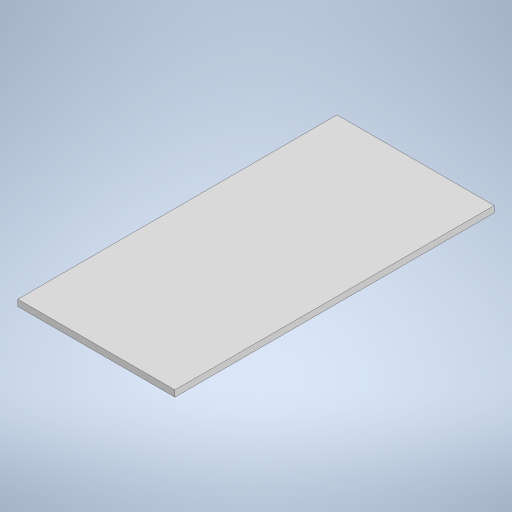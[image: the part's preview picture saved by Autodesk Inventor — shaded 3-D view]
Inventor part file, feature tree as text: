
AUTODESK INVENTOR PART (.ipt)
format: ipt  version: 2024 (Build 280153000, 153)  size: 204,800 bytes
history: native  units: mm
features: extrude x1, sketch x1
ambient origin geometry x8: Origin, YZ Plane, XZ Plane, XY Plane, X Axis, Y Axis, Z Axis, Center Point
bodies: Solid1 (feature_tree)
feature tree (2):
  extrude  "Extrusion1"  Depth=50.0mm
  sketch  "Sketch1"  dims[d0=101.6mm d1=50.0mm d2=2.0mm d3=0.0mm]
